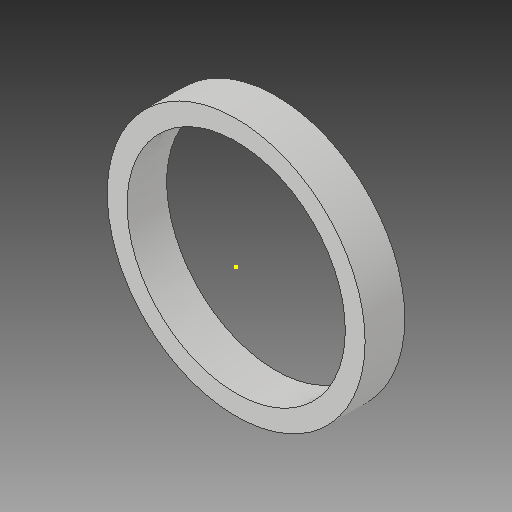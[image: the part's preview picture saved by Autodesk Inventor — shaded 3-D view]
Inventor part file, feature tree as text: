
AUTODESK INVENTOR PART (.ipt)
format: ipt  version: 2019 (Build 230136000, 136)  size: 96,768 bytes
history: native  units: in
note: dims shown in document units (in); Inventor stores cm internally (conversion verified against a paired STEP export)
features: sketch x2, extrude x1
ambient origin geometry x8: Origin, YZ Plane, XZ Plane, XY Plane, X Axis, Y Axis, Z Axis, Center Point
bodies: Solid1 (feature_tree)
feature tree (3):
  extrude  "Extrusion1"  Depth=0.65in
  sketch  "Sketch2"  dims[d2=0.1in d3=0.0in]
  sketch  "Sketch1"  dims[d0=0.55in d1=0.65in]
